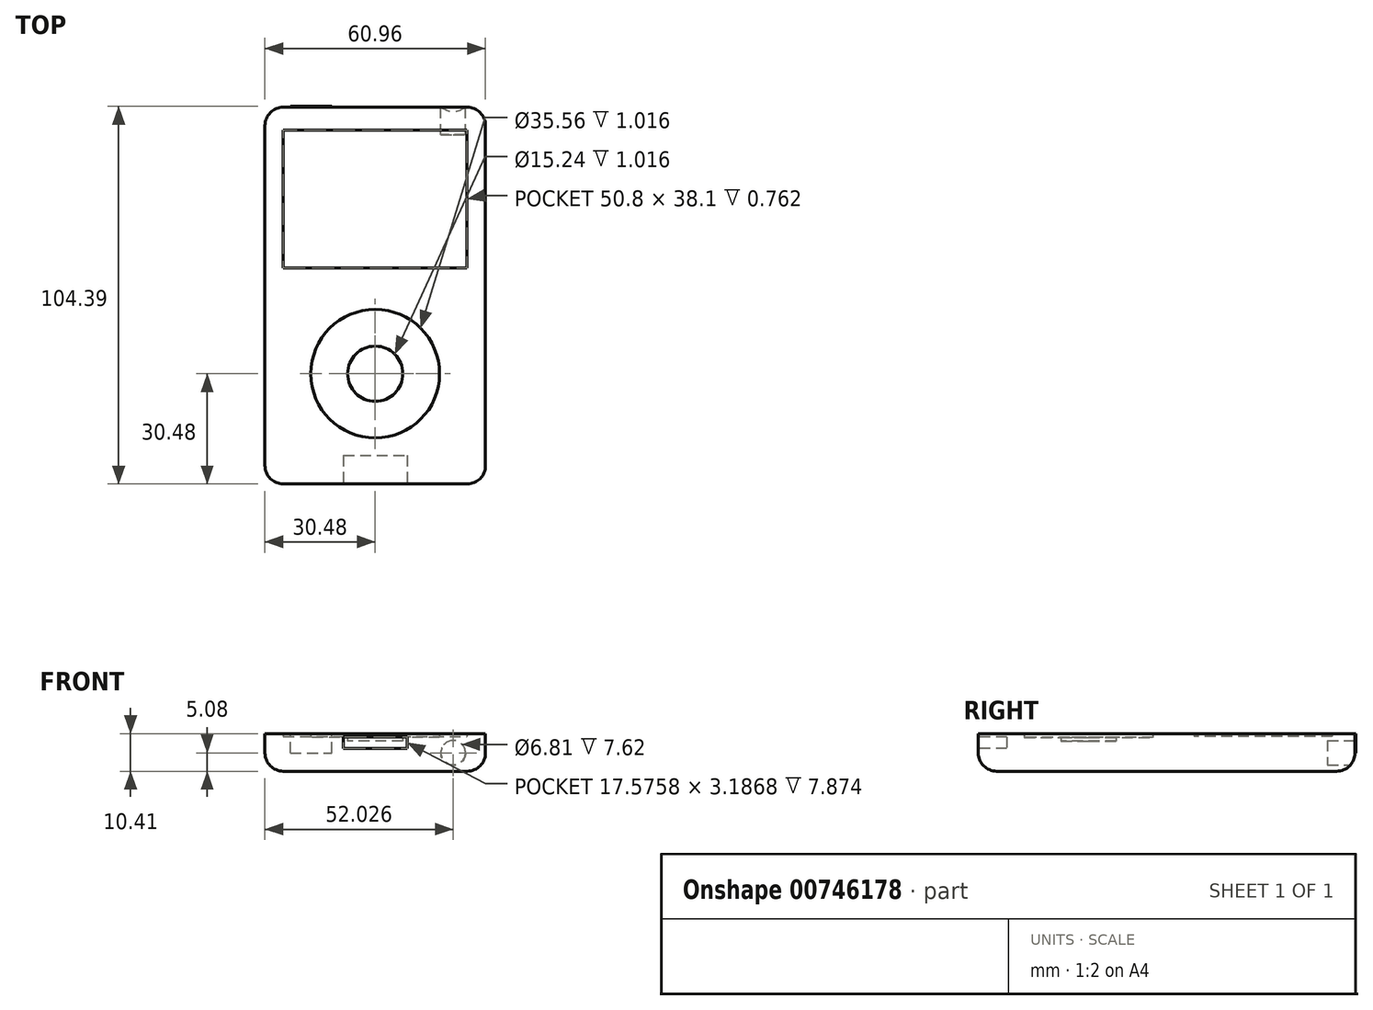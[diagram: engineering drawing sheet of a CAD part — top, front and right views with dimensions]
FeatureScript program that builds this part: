
annotation { "Feature Type Name" : "Feature", "Feature Type Description" : "" }
export const myFeature = defineFeature(function(context is Context, id is Id, definition is map)
    precondition{}
    {
        {
            var Q0;
            Q0=qCreatedBy(makeId("Top.planeOp"),FACE);
            var sketch = newSketch(context, id + "F0", { "sketchPlane" : qUnion([Q0])});
            skLineSegment(sketch, "E0.bottom", {"start": v(-25.4, 52.07) * mm, "end": v(25.4, 52.07) * mm});
            skLineSegment(sketch, "E0.top", {"start": v(-25.4, -52.07) * mm, "end": v(25.4, -52.07) * mm});
            skLineSegment(sketch, "E0.left", {"start": v(-30.48, 47) * mm, "end": v(-30.48, -46.99) * mm});
            skLineSegment(sketch, "E0.right", {"start": v(30.48, 47) * mm, "end": v(30.48, -46.99) * mm});
            skPoint(sketch, "E0.middle", {"position": v(0, 0) * mm});
            skPoint(sketch, "E1.visualSharp", {"position": v(30.48, 52.07) * mm});
            skArc(sketch, "E1.filletArc", {"start": v(30.48, 47) * mm, "mid": v(29, 50.58) * mm, "end": v(25.4, 52.07) * mm});
            skPoint(sketch, "E2.visualSharp", {"position": v(-30.48, 52.07) * mm});
            skArc(sketch, "E2.filletArc", {"start": v(-25.4, 52.07) * mm, "mid": v(-29, 50.58) * mm, "end": v(-30.48, 47) * mm});
            skPoint(sketch, "E3.visualSharp", {"position": v(-30.48, -52.07) * mm});
            skArc(sketch, "E3.filletArc", {"start": v(-30.48, -46.99) * mm, "mid": v(-29, -50.58) * mm, "end": v(-25.4, -52.07) * mm});
            skPoint(sketch, "E4.visualSharp", {"position": v(30.48, -52.07) * mm});
            skArc(sketch, "E4.filletArc", {"start": v(25.4, -52.07) * mm, "mid": v(29, -50.58) * mm, "end": v(30.48, -46.99) * mm});
            skCircle(sketch, "E5", {"center": v(0, -21.59) * mm, "radius": 17.78 * mm});
            skCircle(sketch, "E6", {"center": v(0, -21.59) * mm, "radius": 7.62 * mm});
            skLineSegment(sketch, "E7.bottom", {"start": v(-25.4, 45.72) * mm, "end": v(25.4, 45.72) * mm});
            skLineSegment(sketch, "E7.top", {"start": v(-25.4, 7.62) * mm, "end": v(25.4, 7.62) * mm});
            skLineSegment(sketch, "E7.left", {"start": v(-25.4, 45.72) * mm, "end": v(-25.4, 7.62) * mm});
            skLineSegment(sketch, "E7.right", {"start": v(25.4, 45.72) * mm, "end": v(25.4, 7.62) * mm});
            skPoint(sketch, "E7.middle", {"position": v(0, 26.67) * mm});
            skSolve(sketch);
        }
        {
            var Q0;
            Q0 = qSketchRegion(id + "F0", true);
            extrude(context, id + "F1", {"entities" : qUnion([Q0]), "depth" : 10.4 * mm, "offsetDistance" : 25.4 * mm});
        }
        {
            var Q0;
            Q0=makeQuery(id+"F0.imprint","IMPRINT",FACE,{"disambiguationData":[TD([[makeQuery(id+"F0.imprint","IMPRINT",EDGE,{"derivedFrom":sQuery(id+"F0.wireOp",EDGE,"E7.bottom")}),-1.0]])]});
            extrude(context, id + "F2", {"entities" : qUnion([Q0]), "operationType" : NewBodyOperationType.ADD, "depth" : 9.65 * mm, "offsetDistance" : 25.4 * mm});
        }
        {
            var Q0;
            Q0=makeQuery(id+"F0.imprint","IMPRINT",FACE,{"disambiguationData":[TD([[makeQuery(id+"F0.imprint","IMPRINT",EDGE,{"derivedFrom":sQuery(id+"F0.wireOp",EDGE,"E5")}),1.0]])]});
            extrude(context, id + "F3", {"entities" : qUnion([Q0]), "operationType" : NewBodyOperationType.ADD, "depth" : 9.4 * mm, "offsetDistance" : 25.4 * mm});
        }
        {
            var Q0;
            Q0=makeQuery(id+"F0.imprint","IMPRINT",FACE,{"disambiguationData":[TD([[makeQuery(id+"F0.imprint","IMPRINT",EDGE,{"derivedFrom":sQuery(id+"F0.wireOp",EDGE,"E6")}),1.0]])]});
            extrude(context, id + "F4", {"entities" : qUnion([Q0]), "operationType" : NewBodyOperationType.ADD, "depth" : 8.38 * mm, "offsetDistance" : 25.4 * mm});
        }
        {
            var Q0;
            Q0=makeQuery(id+"F1.opExtrude","CAP_EDGE",EDGE,{"disambiguationData":[OSD([sQuery(id+"F0.wireOp",EDGE,"E3.filletArc")])],"isStart":true});
            fillet(context, id + "F5", {"entities" : qUnion([Q0]), "radius" : 5.08 * mm, "tangentPropagation" : true, "allowEdgeOverflow" : false});
        }
        {
            var Q0;
            Q0=makeQuery(id+"F1.opExtrude","SWEPT_FACE",FACE,{"disambiguationData":[OSD([sQuery(id+"F0.wireOp",EDGE,"E0.top")])]});
            var sketch = newSketch(context, id + "F6", { "sketchPlane" : qUnion([Q0])});
            skLineSegment(sketch, "E8.bottom", {"start": v(-8.79, 9.51) * mm, "end": v(8.79, 9.51) * mm});
            skLineSegment(sketch, "E8.top", {"start": v(-8.79, 6.32) * mm, "end": v(8.79, 6.32) * mm});
            skLineSegment(sketch, "E8.left", {"start": v(-8.79, 9.51) * mm, "end": v(-8.79, 6.32) * mm});
            skLineSegment(sketch, "E8.right", {"start": v(8.79, 9.51) * mm, "end": v(8.79, 6.32) * mm});
            skPoint(sketch, "E8.middle", {"position": v(0, 7.92) * mm});
            skSolve(sketch);
        }
        {
            var Q0;
            Q0=makeQuery(id+"F6.imprint","IMPRINT",FACE,{"disambiguationData":[TD([[makeQuery(id+"F6.imprint","IMPRINT",EDGE,{"derivedFrom":sQuery(id+"F6.wireOp",EDGE,"E8.bottom")}),-1.0]])]});
            extrude(context, id + "F7", {"entities" : qUnion([Q0]), "operationType" : NewBodyOperationType.REMOVE, "oppositeDirection" : true, "depth" : 7.87 * mm, "offsetDistance" : 25.4 * mm});
        }
        {
            var Q0;
            Q0=makeQuery(id+"F1.opExtrude","SWEPT_FACE",FACE,{"disambiguationData":[OSD([sQuery(id+"F0.wireOp",EDGE,"E0.bottom")])]});
            var sketch = newSketch(context, id + "F8", { "sketchPlane" : qUnion([Q0])});
            skLineSegment(sketch, "E9.bottom", {"start": v(11.95, 5.08) * mm, "end": v(23.45, 5.08) * mm});
            skLineSegment(sketch, "E9.top", {"start": v(11.95, 10.35) * mm, "end": v(23.45, 10.35) * mm});
            skLineSegment(sketch, "E9.left", {"start": v(11.95, 5.08) * mm, "end": v(11.95, 10.35) * mm});
            skLineSegment(sketch, "E9.right", {"start": v(23.45, 5.08) * mm, "end": v(23.45, 10.35) * mm});
            skPoint(sketch, "E9.middle", {"position": v(17.7, 7.71) * mm});
            skCircle(sketch, "E10", {"center": v(-21.55, 5.08) * mm, "radius": 3.4 * mm});
            skSolve(sketch);
        }
        {
            var Q0;
            Q0=makeQuery(id+"F8.imprint","IMPRINT",FACE,{"disambiguationData":[TD([[makeQuery(id+"F8.imprint","IMPRINT",EDGE,{"derivedFrom":sQuery(id+"F8.wireOp",EDGE,"E9.bottom")}),1.0]])]});
            extrude(context, id + "F9", {"entities" : qUnion([Q0]), "operationType" : NewBodyOperationType.ADD, "depth" : 0.25 * mm, "offsetDistance" : 25.4 * mm});
        }
        {
            var Q0;
            {var subQ0=sQuery(id+"F8.wireOp",EDGE,"E10");var subQ1=sQuery(id+"F0.wireOp",EDGE,"E0.bottom");var subQ2=makeQuery(id+"F5.opFillet","BLEND_EDGE",EDGE,{"blendedFrom":[makeQuery(id+"F1.opExtrude","CAP_EDGE",EDGE,{"disambiguationData":[OSD([subQ1])],"isStart":true}),makeQuery(id+"F1.opExtrude","SWEPT_FACE",FACE,{"disambiguationData":[OSD([subQ1])]})],"blendedInto":[makeQuery(id+"F1.opExtrude","SWEPT_FACE",FACE,{"disambiguationData":[OSD([subQ1])]})]});var subQ3=makeQuery(id+"F8.imprint","INTERSECT",VERTEX,{"disambiguationData":[OD(0.0)],"derivedFrom":[subQ2,subQ0]});Q0=makeQuery(id+"F8.imprint","IMPRINT",FACE,{"disambiguationData":[TD([[makeQuery(id+"F8.imprint","IMPRINT",EDGE,{"disambiguationData":[TD([[subQ3,-1.0]])],"derivedFrom":subQ0}),1.0]])]});}
            var Q1;
            {var subQ0=sQuery(id+"F8.wireOp",EDGE,"E10");var subQ1=sQuery(id+"F0.wireOp",EDGE,"E0.bottom");var subQ2=makeQuery(id+"F5.opFillet","BLEND_EDGE",EDGE,{"blendedFrom":[makeQuery(id+"F1.opExtrude","CAP_EDGE",EDGE,{"disambiguationData":[OSD([subQ1])],"isStart":true}),makeQuery(id+"F1.opExtrude","SWEPT_FACE",FACE,{"disambiguationData":[OSD([subQ1])]})],"blendedInto":[makeQuery(id+"F1.opExtrude","SWEPT_FACE",FACE,{"disambiguationData":[OSD([subQ1])]})]});var subQ3=makeQuery(id+"F8.imprint","INTERSECT",VERTEX,{"disambiguationData":[OD(0.0)],"derivedFrom":[subQ2,subQ0]});Q1=makeQuery(id+"F8.imprint","IMPRINT",FACE,{"disambiguationData":[TD([[makeQuery(id+"F8.imprint","IMPRINT",EDGE,{"disambiguationData":[TD([[subQ3,1.0]])],"derivedFrom":subQ0}),1.0]])]});}
            extrude(context, id + "F10", {"entities" : qUnion([Q0, Q1]), "operationType" : NewBodyOperationType.REMOVE, "oppositeDirection" : true, "depth" : 7.62 * mm, "offsetDistance" : 25.4 * mm});
        }
    });
